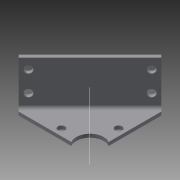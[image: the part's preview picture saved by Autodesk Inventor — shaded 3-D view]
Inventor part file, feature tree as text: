
AUTODESK INVENTOR PART (.ipt)
format: ipt  version: 2013 (Build 170138000, 138)  size: 140,288 bytes
history: native  units: in
note: dims shown in document units (in); Inventor stores cm internally (conversion verified against a paired STEP export)
features: sheet_metal_op x4, other x4, sketch x3
ambient origin geometry x8: Origin, YZ Plane, XZ Plane, XY Plane, X Axis, Y Axis, Z Axis, Center Point
bodies: Solid1 (feature_tree)
feature tree (11):
  sheet_metal_op  "Face1"
  sheet_metal_op  "Flange1"
  sketch  "Sketch3"  dims[d2=0.26in d3=0.26in d4=0.26in d5=1.0in d8=0.25in d9=0.0in d10=0.25in d11=0.25in d12=45.0deg d13=0.75in d14=0.125in d15=0.125in d16=0.0625in d17=0.25in d18=0.125in d19=1.75in d20=90.0deg d21=0.125in d22=0.5in d23=0.125in d24=0.125in d35=3.685in d36=0.266in d37=0.266in d38=0.266in d39=0.266in d40=0.25in d41=0.375in d42=0.375in d43=0.25in d44=0.375in d45=0.375in d47=0.25in d48=0.25in d49=0.125in d50=0.0in]
  other  "Work Axis1"
  sketch  "Sketch1"  dims[d0=2.09in]
  other  "Plate1"
  sketch  "Sketch2"  dims[d1=0.26in]
  other  "Plate2"
  sheet_metal_op  "Bend1"
  sheet_metal_op  "Corner1"
  other  "Cut3"
